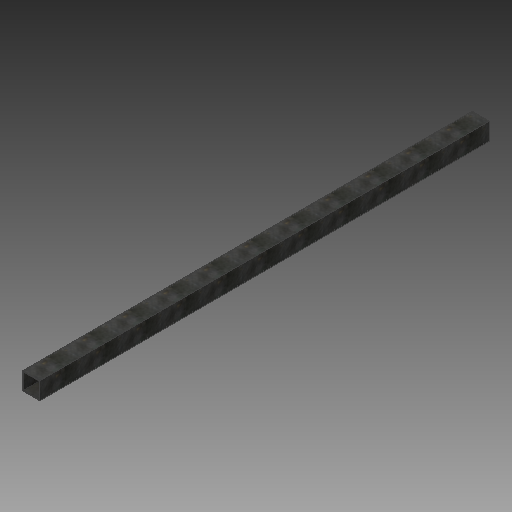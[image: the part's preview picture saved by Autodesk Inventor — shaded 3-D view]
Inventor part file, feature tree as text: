
AUTODESK INVENTOR PART (.ipt)
format: ipt  version: 2018 (Build 220112000, 112)  size: 116,224 bytes
history: native  units: mm
features: other x1, extrude x1, sketch x1
ambient origin geometry x8: Origin, YZ Plane, XZ Plane, XY Plane, X Axis, Y Axis, Z Axis, Center Point
bodies: Body1 (feature_tree)
feature tree (3):
  other  "Sólido1"
  extrude  "Extrusión1"  Depth=75.0mm
  sketch  "Boceto1"  dims[d0=75.0mm d1=75.0mm d2=3.0mm d3=37.5mm d4=37.5mm d5=1950.0mm d6=0.0mm]
